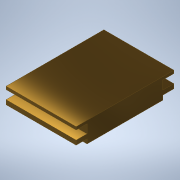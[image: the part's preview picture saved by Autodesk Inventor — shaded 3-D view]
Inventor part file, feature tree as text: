
AUTODESK INVENTOR PART (.ipt)
format: ipt  version: 2022 (Build 260153000, 153)  size: 145,408 bytes
history: native  units: in
note: dims shown in document units (in); Inventor stores cm internally (conversion verified against a paired STEP export)
features: extrude x3, sketch x3
ambient origin geometry x8: Origin, YZ Plane, XZ Plane, XY Plane, X Axis, Y Axis, Z Axis, Center Point
bodies: Solid1 (feature_tree)
feature tree (6):
  extrude  "Extrusion1"  Depth=1.8898in
  extrude  "Extrusion4"  Depth=0.0787in
  extrude  "Extrusion5"  Depth=0.1181in
  sketch  "Sketch1"  dims[d0=2.0472in d1=1.8898in]
  sketch  "Sketch4"  dims[d2=0.5512in d3=0.0in d14=0.0787in]
  sketch  "Sketch5"  dims[d15=0.1181in d16=0.1181in d17=0.2953in d18=0.0in d21=0.1181in d22=0.2953in d23=0.0in]
